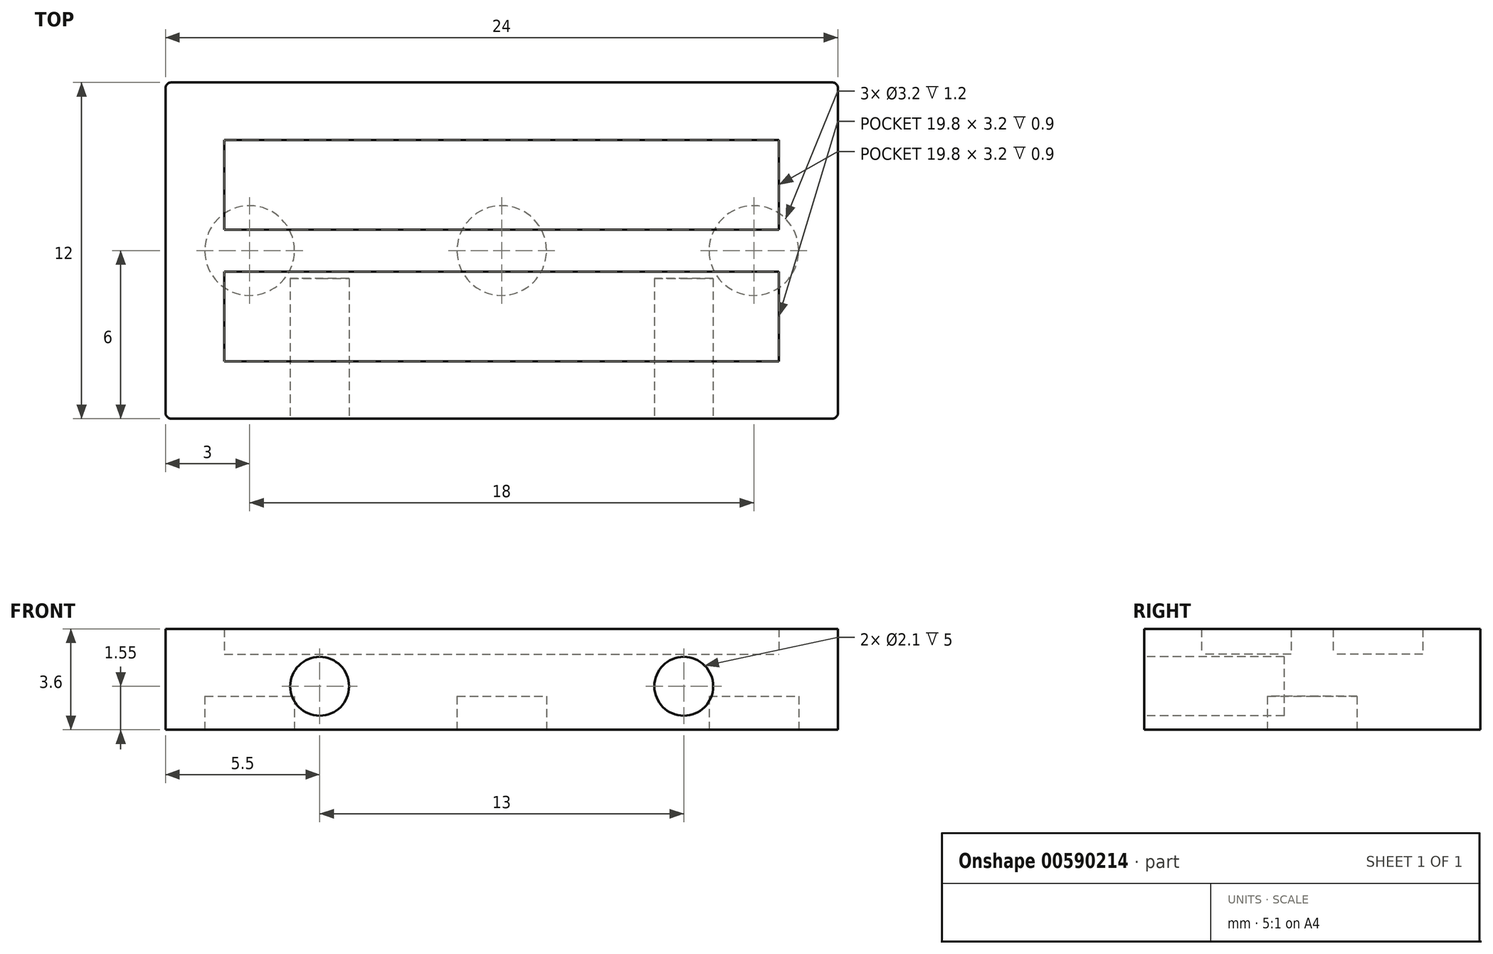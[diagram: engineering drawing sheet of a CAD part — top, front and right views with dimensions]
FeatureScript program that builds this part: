
annotation { "Feature Type Name" : "Feature", "Feature Type Description" : "" }
export const myFeature = defineFeature(function(context is Context, id is Id, definition is map)
    precondition{}
    {
        {
            var Q0;
            Q0=qCreatedBy(makeId("Top.planeOp"),FACE);
            var sketch = newSketch(context, id + "F0", { "sketchPlane" : qUnion([Q0])});
            skPoint(sketch, "E0.middle", {"position": v(0, 0) * mm});
            skLineSegment(sketch, "E1.bottom", {"start": v(-9.9, 3.95) * mm, "end": v(9.9, 3.95) * mm});
            skLineSegment(sketch, "E1.top", {"start": v(-9.9, 0.75) * mm, "end": v(9.9, 0.75) * mm});
            skLineSegment(sketch, "E1.left", {"start": v(-9.9, 3.95) * mm, "end": v(-9.9, 0.75) * mm});
            skLineSegment(sketch, "E1.right", {"start": v(9.9, 3.95) * mm, "end": v(9.9, 0.75) * mm});
            skPoint(sketch, "E1.middle", {"position": v(0, 2.35) * mm});
            skLineSegment(sketch, "E2.bottom", {"start": v(-9.9, -0.75) * mm, "end": v(9.9, -0.75) * mm});
            skLineSegment(sketch, "E2.top", {"start": v(-9.9, -3.95) * mm, "end": v(9.9, -3.95) * mm});
            skLineSegment(sketch, "E2.left", {"start": v(-9.9, -0.75) * mm, "end": v(-9.9, -3.95) * mm});
            skLineSegment(sketch, "E2.right", {"start": v(9.9, -0.75) * mm, "end": v(9.9, -3.95) * mm});
            skPoint(sketch, "E2.middle", {"position": v(0, -2.35) * mm});
            skLineSegment(sketch, "E3.bottom", {"start": v(-12, 6) * mm, "end": v(12, 6) * mm});
            skLineSegment(sketch, "E3.top", {"start": v(-12, -6) * mm, "end": v(12, -6) * mm});
            skLineSegment(sketch, "E3.left", {"start": v(-12, 6) * mm, "end": v(-12, -6) * mm});
            skLineSegment(sketch, "E3.right", {"start": v(12, 6) * mm, "end": v(12, -6) * mm});
            skSolve(sketch);
        }
        {
            var Q0;
            Q0=makeQuery(id+"F0.imprint","IMPRINT",FACE,{"disambiguationData":[TD([[makeQuery(id+"F0.imprint","IMPRINT",EDGE,{"derivedFrom":sQuery(id+"F0.wireOp",EDGE,"E1.bottom")}),1.0]])]});
            extrude(context, id + "F1", {"entities" : qUnion([Q0]), "depth" : .9 * mm, "offsetDistance" : 25 * mm});
        }
        {
            var Q0;
            Q0=makeQuery(id+"F1.opExtrude","CAP_FACE",FACE,{"disambiguationData":[OSD([sQuery(id+"F0.wireOp",EDGE,"E1.bottom"),sQuery(id+"F0.wireOp",EDGE,"E1.top"),sQuery(id+"F0.wireOp",EDGE,"E1.left"),sQuery(id+"F0.wireOp",EDGE,"E1.right"),sQuery(id+"F0.wireOp",EDGE,"E2.bottom"),sQuery(id+"F0.wireOp",EDGE,"E2.top"),sQuery(id+"F0.wireOp",EDGE,"E2.left"),sQuery(id+"F0.wireOp",EDGE,"E2.right"),sQuery(id+"F0.wireOp",EDGE,"E3.bottom"),sQuery(id+"F0.wireOp",EDGE,"E3.top"),sQuery(id+"F0.wireOp",EDGE,"E3.left"),sQuery(id+"F0.wireOp",EDGE,"E3.right")])],"isStart":true});
            var sketch = newSketch(context, id + "F2", { "sketchPlane" : qUnion([Q0])});
            skLineSegment(sketch, "E4.bottom", {"start": v(12, 6) * mm, "end": v(-12, 6) * mm});
            skLineSegment(sketch, "E4.top", {"start": v(12, -6) * mm, "end": v(-12, -6) * mm});
            skLineSegment(sketch, "E4.left", {"start": v(12, 6) * mm, "end": v(12, -6) * mm});
            skLineSegment(sketch, "E4.right", {"start": v(-12, 6) * mm, "end": v(-12, -6) * mm});
            skPoint(sketch, "E4.middle", {"position": v(0, 0) * mm});
            skSolve(sketch);
        }
        {
            var Q0;
            Q0 = qSketchRegion(id + "F2", true);
            extrude(context, id + "F3", {"entities" : qUnion([Q0]), "operationType" : NewBodyOperationType.ADD, "depth" : 2.7 * mm, "offsetDistance" : 25 * mm});
        }
        {
            var Q0;
            Q0=makeQuery(id+"F3.opExtrude","CAP_FACE",FACE,{"disambiguationData":[OSD([sQuery(id+"F2.wireOp",EDGE,"E4.bottom"),sQuery(id+"F2.wireOp",EDGE,"E4.top"),sQuery(id+"F2.wireOp",EDGE,"E4.left"),sQuery(id+"F2.wireOp",EDGE,"E4.right")])],"isStart":false});
            var sketch = newSketch(context, id + "F4", { "sketchPlane" : qUnion([Q0])});
            skCircle(sketch, "E5", {"center": v(0, 0) * mm, "radius": 1.6 * mm});
            skCircle(sketch, "E6", {"center": v(-9, 0) * mm, "radius": 1.6 * mm});
            skCircle(sketch, "E7", {"center": v(9, 0) * mm, "radius": 1.6 * mm});
            skSolve(sketch);
        }
        {
            var Q0;
            Q0 = qSketchRegion(id + "F4", true);
            extrude(context, id + "F5", {"entities" : qUnion([Q0]), "operationType" : NewBodyOperationType.REMOVE, "oppositeDirection" : true, "depth" : 1.2 * mm, "offsetDistance" : 25 * mm});
        }
        {
            var Q0;
            Q0=makeQuery(id+"F3.boolean.opBoolean","MERGE",EDGE,{"derivedFrom":[makeQuery(id+"F1.opExtrude","SWEPT_EDGE",EDGE,{"disambiguationData":[OSD([sQuery(id+"F0.wireOp",EDGE,"E3.top"),sQuery(id+"F0.wireOp",EDGE,"E3.left")])]}),makeQuery(id+"F3.opExtrude","SWEPT_EDGE",EDGE,{"disambiguationData":[OSD([sQuery(id+"F2.wireOp",EDGE,"E4.bottom"),sQuery(id+"F2.wireOp",EDGE,"E4.right")])]})]});
            var Q1;
            Q1=makeQuery(id+"F3.boolean.opBoolean","MERGE",EDGE,{"derivedFrom":[makeQuery(id+"F1.opExtrude","SWEPT_EDGE",EDGE,{"disambiguationData":[OSD([sQuery(id+"F0.wireOp",EDGE,"E3.bottom"),sQuery(id+"F0.wireOp",EDGE,"E3.left")])]}),makeQuery(id+"F3.opExtrude","SWEPT_EDGE",EDGE,{"disambiguationData":[OSD([sQuery(id+"F2.wireOp",EDGE,"E4.top"),sQuery(id+"F2.wireOp",EDGE,"E4.right")])]})]});
            var Q2;
            Q2=makeQuery(id+"F3.boolean.opBoolean","MERGE",EDGE,{"derivedFrom":[makeQuery(id+"F1.opExtrude","SWEPT_EDGE",EDGE,{"disambiguationData":[OSD([sQuery(id+"F0.wireOp",EDGE,"E3.bottom"),sQuery(id+"F0.wireOp",EDGE,"E3.right")])]}),makeQuery(id+"F3.opExtrude","SWEPT_EDGE",EDGE,{"disambiguationData":[OSD([sQuery(id+"F2.wireOp",EDGE,"E4.top"),sQuery(id+"F2.wireOp",EDGE,"E4.left")])]})]});
            var Q3;
            Q3=makeQuery(id+"F3.boolean.opBoolean","MERGE",EDGE,{"derivedFrom":[makeQuery(id+"F1.opExtrude","SWEPT_EDGE",EDGE,{"disambiguationData":[OSD([sQuery(id+"F0.wireOp",EDGE,"E3.top"),sQuery(id+"F0.wireOp",EDGE,"E3.right")])]}),makeQuery(id+"F3.opExtrude","SWEPT_EDGE",EDGE,{"disambiguationData":[OSD([sQuery(id+"F2.wireOp",EDGE,"E4.bottom"),sQuery(id+"F2.wireOp",EDGE,"E4.left")])]})]});
            fillet(context, id + "F6", {"entities" : qUnion([Q0, Q1, Q2, Q3]), "radius" : .2 * mm, "tangentPropagation" : true, "allowEdgeOverflow" : false});
        }
        {
            var Q0;
            Q0=makeQuery(id+"F3.boolean.opBoolean","MERGE",FACE,{"derivedFrom":[makeQuery(id+"F1.opExtrude","SWEPT_FACE",FACE,{"disambiguationData":[OSD([sQuery(id+"F0.wireOp",EDGE,"E3.top")])]}),makeQuery(id+"F3.opExtrude","SWEPT_FACE",FACE,{"disambiguationData":[OSD([sQuery(id+"F2.wireOp",EDGE,"E4.bottom")])]})]});
            var sketch = newSketch(context, id + "F7", { "sketchPlane" : qUnion([Q0])});
            skCircle(sketch, "E8", {"center": v(-6.5, -1.15) * mm, "radius": 1.05 * mm});
            skCircle(sketch, "E9", {"center": v(6.5, -1.15) * mm, "radius": 1.05 * mm});
            skSolve(sketch);
        }
        {
            var Q0;
            Q0 = qSketchRegion(id + "F7", true);
            extrude(context, id + "F8", {"entities" : qUnion([Q0]), "operationType" : NewBodyOperationType.REMOVE, "oppositeDirection" : true, "depth" : 5 * mm, "offsetDistance" : 25 * mm});
        }
    });
